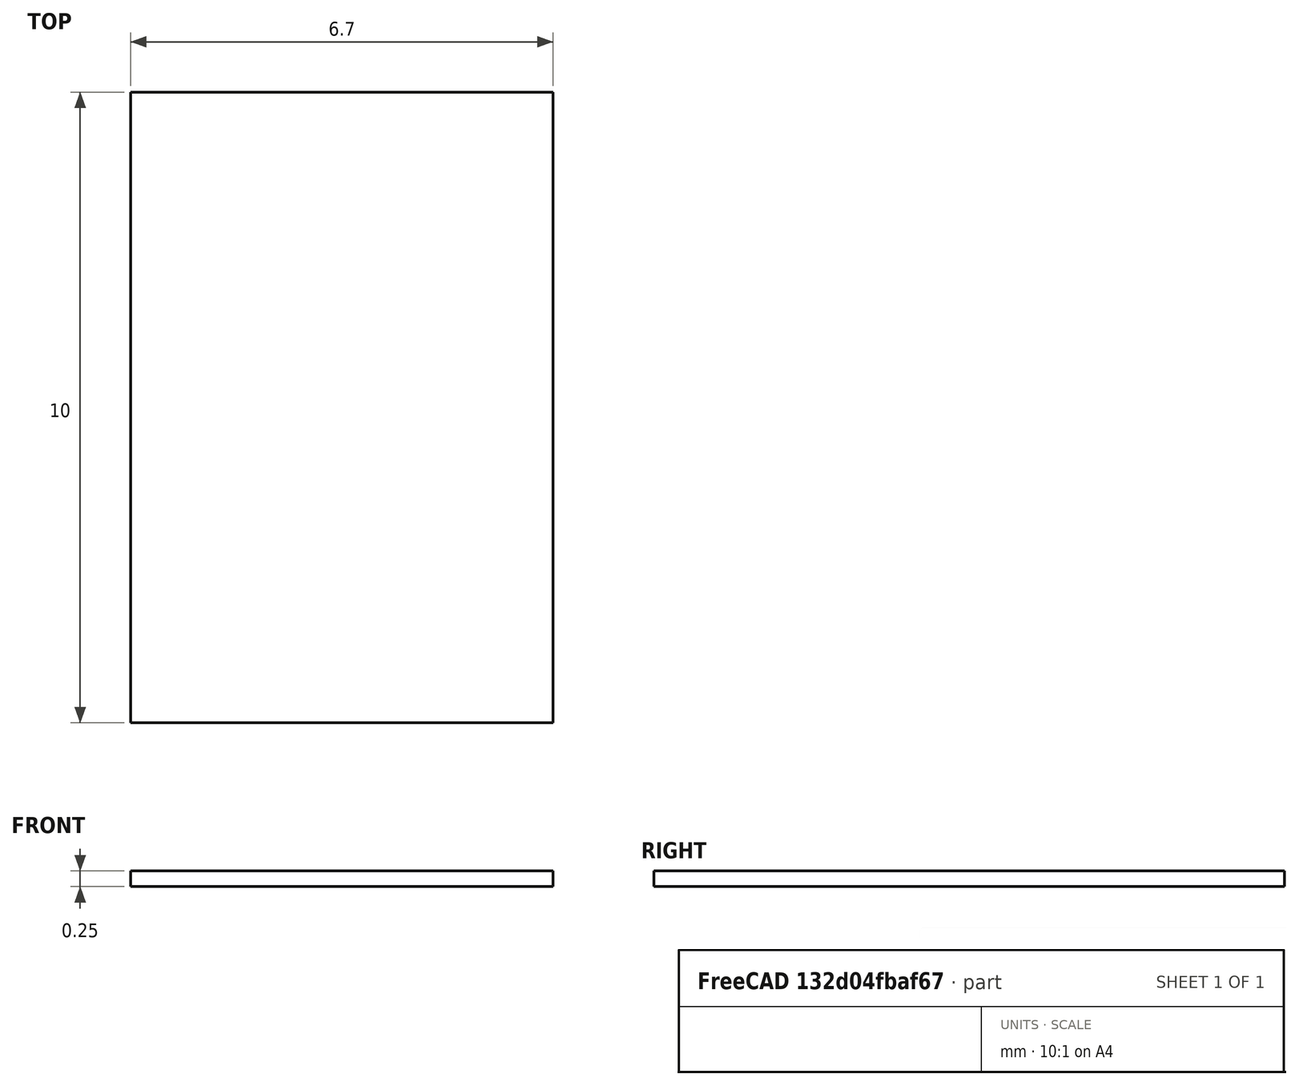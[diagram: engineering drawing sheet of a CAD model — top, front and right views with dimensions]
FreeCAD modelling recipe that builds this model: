
FCSTD DOCUMENT  (FreeCAD 0.18.4R)
Label: Sample_Holder_PCB_Dummy_v1
License: All rights reserved
LicenseURL: http://en.wikipedia.org/wiki/All_rights_reserved
objects: Sketcher::SketchObject×1, PartDesign::Pad×1, PartDesign::Body×1
note: 4 computed .brp shape members not serialized (recipe doc carries the construction recipe); baked Part::Feature solids carry a one-line shape summary decoded from their .brp

FEATURE [Sketcher::SketchObject] Sketch
  MapMode = 5
  Support = -> [XY_Plane]
  sketch-geometry (4):
    g0: LineSegment StartX=-3.4 StartY=5 StartZ=0 EndX=3.3 EndY=5 EndZ=0
    g1: LineSegment StartX=3.3 StartY=5 StartZ=0 EndX=3.3 EndY=-5 EndZ=0
    g2: LineSegment StartX=3.3 StartY=-5 StartZ=0 EndX=-3.4 EndY=-5 EndZ=0
    g3: LineSegment StartX=-3.4 StartY=-5 StartZ=0 EndX=-3.4 EndY=5 EndZ=0
  constraints (12):
    c: Coincident(g0,g1)
    c: Coincident(g1,g2)
    c: Coincident(g2,g3)
    c: Coincident(g3,g0)
    c: Horizontal(g0)
    c: Horizontal(g2)
    c: Vertical(g1)
    c: Vertical(g3)
    c: DistanceY(g1,g1) = 10
    c: DistanceX(g0,g0) = 6.7
    c: DistanceY(g-1,g0) = 5
    c: DistanceX(g-1,g0) = -3.4
FEATURE [PartDesign::Pad] Pad
  Length = 0.25
  Length2 = 100
  Profile = -> Sketch
  Type = 0
FEATURE [PartDesign::Body] Body
  Group = -> [Sketch,Pad]
  Origin = -> Origin
  Tip = -> Pad
